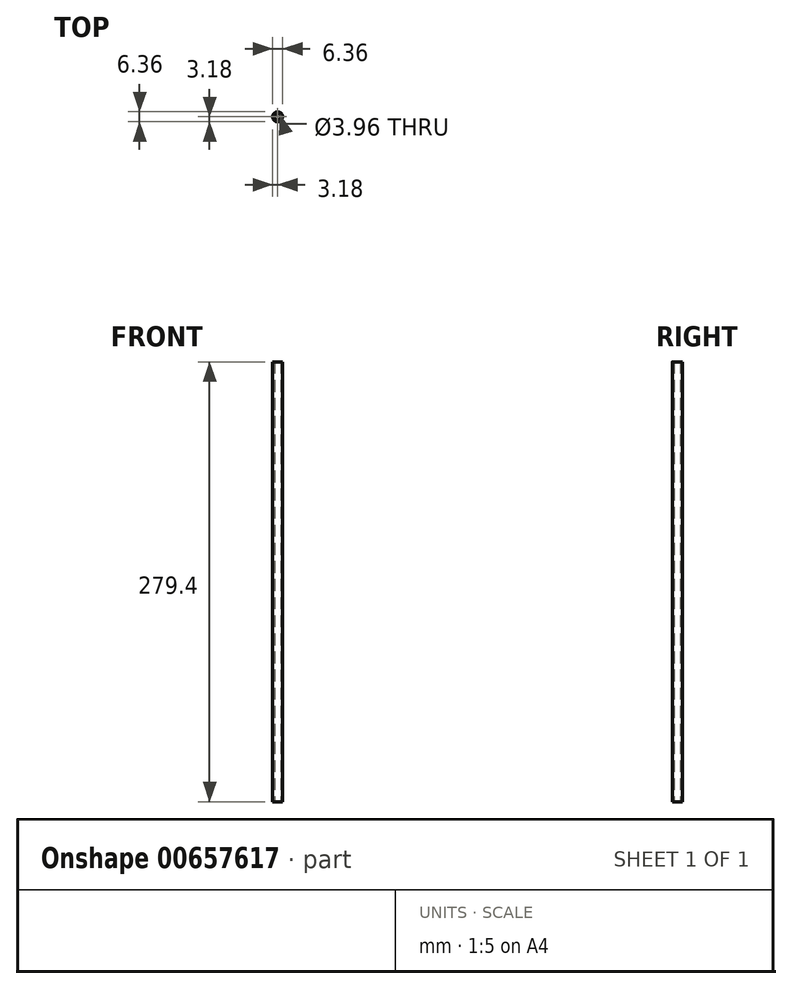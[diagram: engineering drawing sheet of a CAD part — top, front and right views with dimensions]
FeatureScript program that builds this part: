
annotation { "Feature Type Name" : "Feature", "Feature Type Description" : "" }
export const myFeature = defineFeature(function(context is Context, id is Id, definition is map)
    precondition{}
    {
        {
            var Q0;
            Q0=qCreatedBy(makeId("Top.planeOp"),FACE);
            var sketch = newSketch(context, id + "F0", { "sketchPlane" : qUnion([Q0])});
            skCircle(sketch, "E0", {"center": v(0, 0) * mm, "radius": 3.18 * mm});
            skCircle(sketch, "E1", {"center": v(0, 0) * mm, "radius": 1.98 * mm});
            skSolve(sketch);
        }
        {
            var Q0;
            Q0 = qSketchRegion(id + "F0", true);
            extrude(context, id + "F1", {"entities" : qUnion([Q0]), "depth" : 279.4 * mm, "offsetDistance" : 25.4 * mm});
        }
    });
